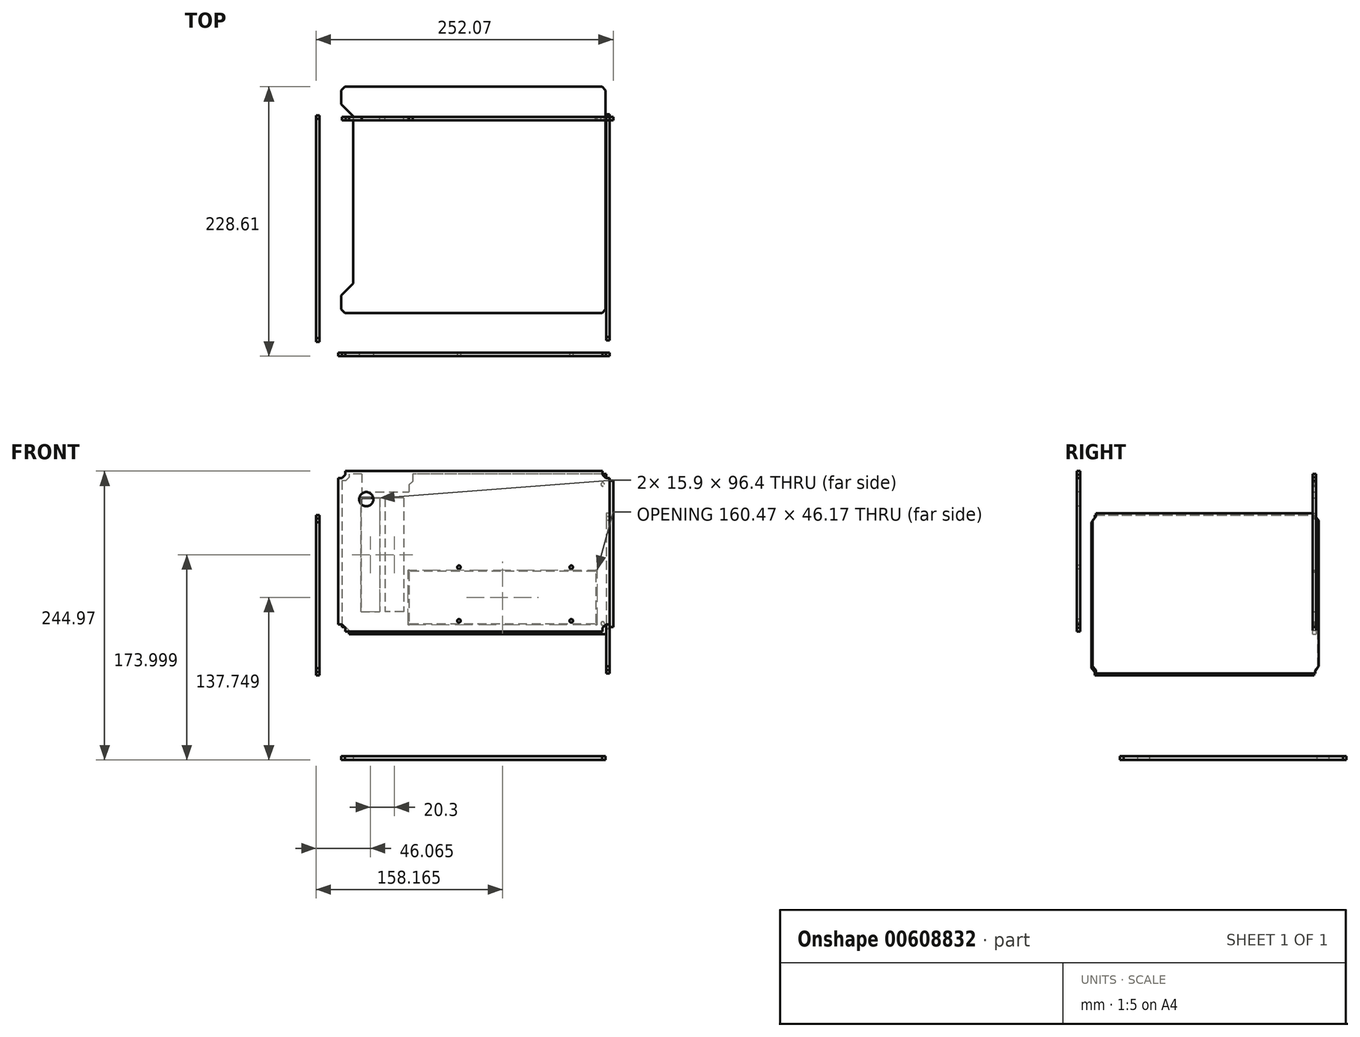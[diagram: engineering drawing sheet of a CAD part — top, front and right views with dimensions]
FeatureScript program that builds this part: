
annotation { "Feature Type Name" : "Feature", "Feature Type Description" : "" }
export const myFeature = defineFeature(function(context is Context, id is Id, definition is map)
    precondition{}
    {
        {
            var Q0;
            Q0=qCreatedBy(makeId("Front.planeOp"),FACE);
            cPlane(context, id + "F0", {"entities" : qUnion([Q0]), "cplaneType" : CPlaneType.OFFSET, "offset" : 80 * mm, "width" : 150 * mm, "height" : 150 * mm});
        }
        {
            var Q0;
            Q0=qCreatedBy(id+"F0.planeOp",FACE);
            var sketch = newSketch(context, id + "F1", { "sketchPlane" : qUnion([Q0])});
            skLineSegment(sketch, "E0.bottom", {"start": v(-107.2, 92.97) * mm, "end": v(122.8, 92.97) * mm});
            skLineSegment(sketch, "E0.top", {"start": v(-107.2, -43.03) * mm, "end": v(122.8, -43.03) * mm});
            skLineSegment(sketch, "E0.left", {"start": v(-107.2, 92.97) * mm, "end": v(-107.2, -43.03) * mm});
            skLineSegment(sketch, "E0.right", {"start": v(122.8, 92.97) * mm, "end": v(122.8, -43.03) * mm});
            skLineSegment(sketch, "E1", {"start": v(116.8, 92.97) * mm, "end": v(116.8, 89.97) * mm});
            skLineSegment(sketch, "E2", {"start": v(116.8, 89.97) * mm, "end": v(119.8, 86.97) * mm});
            skLineSegment(sketch, "E3", {"start": v(119.8, 86.97) * mm, "end": v(122.8, 86.97) * mm});
            skLineSegment(sketch, "E4", {"start": v(122.8, -37.03) * mm, "end": v(119.8, -37.03) * mm});
            skLineSegment(sketch, "E5", {"start": v(119.8, -37.03) * mm, "end": v(116.8, -40.03) * mm});
            skLineSegment(sketch, "E6", {"start": v(116.8, -40.03) * mm, "end": v(116.8, -43.03) * mm});
            skLineSegment(sketch, "E7", {"start": v(-107.2, -37.03) * mm, "end": v(-104.2, -37.03) * mm});
            skLineSegment(sketch, "E8", {"start": v(-104.2, -37.03) * mm, "end": v(-101.2, -40.03) * mm});
            skLineSegment(sketch, "E9", {"start": v(-101.2, -40.03) * mm, "end": v(-101.2, -43.03) * mm});
            skLineSegment(sketch, "E10", {"start": v(-107.2, 86.97) * mm, "end": v(-104.2, 86.97) * mm});
            skLineSegment(sketch, "E11", {"start": v(-104.2, 86.97) * mm, "end": v(-101.2, 89.97) * mm});
            skLineSegment(sketch, "E12", {"start": v(-101.2, 89.97) * mm, "end": v(-101.2, 92.97) * mm});
            skSolve(sketch);
        }
        {
            var Q0;
            {var subQ2=sQuery(id+"F1.wireOp",EDGE,"E1");Q0=makeQuery(id+"F1.imprint","IMPRINT",FACE,{"disambiguationData":[TD([[makeQuery(id+"F1.imprint","IMPRINT",EDGE,{"derivedFrom":subQ2}),-1.0]])]});}
            extrude(context, id + "F2", {"entities" : qUnion([Q0]), "depth" : 3 * mm, "offsetDistance" : 25 * mm});
        }
        {
            var Q0;
            Q0=qCreatedBy(makeId("Right.planeOp"),FACE);
            cPlane(context, id + "F3", {"entities" : qUnion([Q0]), "cplaneType" : CPlaneType.OFFSET, "offset" : 120 * mm, "width" : 150 * mm, "height" : 150 * mm});
        }
        {
            var Q0;
            Q0=qCreatedBy(id+"F3.planeOp",FACE);
            var sketch = newSketch(context, id + "F4", { "sketchPlane" : qUnion([Q0])});
            skLineSegment(sketch, "E13.bottom", {"start": v(-69.71, 57.33) * mm, "end": v(122.29, 57.33) * mm});
            skLineSegment(sketch, "E13.top", {"start": v(-69.71, -78.67) * mm, "end": v(122.29, -78.67) * mm});
            skLineSegment(sketch, "E13.left", {"start": v(-69.71, 57.33) * mm, "end": v(-69.71, -78.67) * mm});
            skLineSegment(sketch, "E13.right", {"start": v(122.29, 57.33) * mm, "end": v(122.29, -78.67) * mm});
            skLineSegment(sketch, "E14", {"start": v(-66.71, 57.33) * mm, "end": v(-66.71, 54.33) * mm});
            skLineSegment(sketch, "E15", {"start": v(-66.71, 54.33) * mm, "end": v(-69.71, 51.33) * mm});
            skLineSegment(sketch, "E16", {"start": v(-69.71, -72.67) * mm, "end": v(-66.71, -75.67) * mm});
            skLineSegment(sketch, "E17", {"start": v(-66.71, -75.67) * mm, "end": v(-66.71, -78.67) * mm});
            skLineSegment(sketch, "E18", {"start": v(119.29, 57.33) * mm, "end": v(119.29, 54.33) * mm});
            skLineSegment(sketch, "E19", {"start": v(119.29, 54.33) * mm, "end": v(122.29, 51.33) * mm});
            skLineSegment(sketch, "E20", {"start": v(122.29, -72.67) * mm, "end": v(119.29, -75.67) * mm});
            skLineSegment(sketch, "E21", {"start": v(119.29, -75.67) * mm, "end": v(119.29, -78.67) * mm});
            skSolve(sketch);
        }
        {
            var Q0;
            {var subQ4=sQuery(id+"F4.wireOp",EDGE,"E14");Q0=makeQuery(id+"F4.imprint","IMPRINT",FACE,{"disambiguationData":[TD([[makeQuery(id+"F4.imprint","IMPRINT",EDGE,{"derivedFrom":subQ4}),1.0]])]});}
            extrude(context, id + "F5", {"entities" : qUnion([Q0]), "depth" : 3 * mm, "offsetDistance" : 25 * mm});
        }
        {
            var Q0;
            Q0=qCreatedBy(makeId("Front.planeOp"),FACE);
            cPlane(context, id + "F6", {"entities" : qUnion([Q0]), "cplaneType" : CPlaneType.OFFSET, "offset" : 120 * mm, "oppositeDirection" : true, "width" : 150 * mm, "height" : 150 * mm});
        }
        {
            var Q0;
            Q0=qCreatedBy(id+"F6.planeOp",FACE);
            var sketch = newSketch(context, id + "F7", { "sketchPlane" : qUnion([Q0])});
            skLineSegment(sketch, "E22.bottom", {"start": v(126.07, 90.7) * mm, "end": v(-103.93, 90.7) * mm});
            skLineSegment(sketch, "E22.top", {"start": v(126.07, -45.3) * mm, "end": v(-103.93, -45.3) * mm});
            skLineSegment(sketch, "E22.left", {"start": v(126.07, 90.7) * mm, "end": v(126.07, -45.3) * mm});
            skLineSegment(sketch, "E22.right", {"start": v(-103.93, 90.7) * mm, "end": v(-103.93, -45.3) * mm});
            skLineSegment(sketch, "E23", {"start": v(126.07, 84.7) * mm, "end": v(123.07, 84.7) * mm});
            skLineSegment(sketch, "E24", {"start": v(123.07, 84.7) * mm, "end": v(120.07, 87.7) * mm});
            skLineSegment(sketch, "E25", {"start": v(120.07, 87.7) * mm, "end": v(120.07, 90.7) * mm});
            skLineSegment(sketch, "E26", {"start": v(-97.93, 90.7) * mm, "end": v(-97.93, 87.7) * mm});
            skLineSegment(sketch, "E27", {"start": v(-97.93, 87.7) * mm, "end": v(-100.93, 84.7) * mm});
            skLineSegment(sketch, "E28", {"start": v(-100.93, 84.7) * mm, "end": v(-103.93, 84.7) * mm});
            skLineSegment(sketch, "E29", {"start": v(-97.93, -45.3) * mm, "end": v(-97.93, -42.3) * mm});
            skLineSegment(sketch, "E30", {"start": v(-97.93, -42.3) * mm, "end": v(-100.93, -39.3) * mm});
            skLineSegment(sketch, "E31", {"start": v(-100.93, -39.3) * mm, "end": v(-103.93, -39.3) * mm});
            skLineSegment(sketch, "E32", {"start": v(126.07, -39.3) * mm, "end": v(123.07, -39.3) * mm});
            skLineSegment(sketch, "E33", {"start": v(123.07, -39.3) * mm, "end": v(120.07, -42.3) * mm});
            skLineSegment(sketch, "E34", {"start": v(120.07, -42.3) * mm, "end": v(120.07, -45.3) * mm});
            skLineSegment(sketch, "E35", {"start": v(126.07, -36.3) * mm, "end": v(117.07, -36.3) * mm, "construction": true});
            skCircle(sketch, "E36", {"center": v(117.07, -36.3) * mm, "radius": 1.5 * mm});
            skLineSegment(sketch, "E37", {"start": v(126.07, 81.7) * mm, "end": v(117.07, 81.7) * mm, "construction": true});
            skCircle(sketch, "E38", {"center": v(117.07, 81.7) * mm, "radius": 1.5 * mm});
            skSolve(sketch);
        }
        {
            var Q0;
            {var subQ2=sQuery(id+"F7.wireOp",EDGE,"E23");Q0=makeQuery(id+"F7.imprint","IMPRINT",FACE,{"disambiguationData":[TD([[makeQuery(id+"F7.imprint","IMPRINT",EDGE,{"derivedFrom":subQ2}),1.0]])]});}
            extrude(context, id + "F8", {"entities" : qUnion([Q0]), "depth" : 3 * mm, "offsetDistance" : 25 * mm});
        }
        {
            var Q0;
            Q0=qCreatedBy(makeId("Right.planeOp"),FACE);
            cPlane(context, id + "F9", {"entities" : qUnion([Q0]), "cplaneType" : CPlaneType.OFFSET, "offset" : 126 * mm, "oppositeDirection" : true, "width" : 150 * mm, "height" : 150 * mm});
        }
        {
            var Q0;
            Q0=qCreatedBy(id+"F9.planeOp",FACE);
            var sketch = newSketch(context, id + "F10", { "sketchPlane" : qUnion([Q0])});
            skLineSegment(sketch, "E39.bottom", {"start": v(-70.73, 55.68) * mm, "end": v(121.27, 55.68) * mm});
            skLineSegment(sketch, "E39.top", {"start": v(-70.73, -80.32) * mm, "end": v(121.27, -80.32) * mm});
            skLineSegment(sketch, "E39.left", {"start": v(-70.73, 55.68) * mm, "end": v(-70.73, -80.32) * mm});
            skLineSegment(sketch, "E39.right", {"start": v(121.27, 55.68) * mm, "end": v(121.27, -80.32) * mm});
            skLineSegment(sketch, "E40", {"start": v(121.27, 49.68) * mm, "end": v(118.27, 52.68) * mm});
            skLineSegment(sketch, "E41", {"start": v(118.27, 52.68) * mm, "end": v(118.27, 55.68) * mm});
            skLineSegment(sketch, "E42", {"start": v(-67.73, 55.68) * mm, "end": v(-67.73, 52.68) * mm});
            skLineSegment(sketch, "E43", {"start": v(-67.73, 52.68) * mm, "end": v(-70.73, 49.68) * mm});
            skLineSegment(sketch, "E44", {"start": v(-67.73, -80.32) * mm, "end": v(-67.73, -77.32) * mm});
            skLineSegment(sketch, "E45", {"start": v(-67.73, -77.32) * mm, "end": v(-70.73, -74.32) * mm});
            skLineSegment(sketch, "E46", {"start": v(121.27, -74.32) * mm, "end": v(118.27, -77.32) * mm});
            skLineSegment(sketch, "E47", {"start": v(118.27, -77.32) * mm, "end": v(118.27, -80.32) * mm});
            skSolve(sketch);
        }
        {
            var Q0;
            {var subQ4=sQuery(id+"F10.wireOp",EDGE,"E40");Q0=makeQuery(id+"F10.imprint","IMPRINT",FACE,{"disambiguationData":[TD([[makeQuery(id+"F10.imprint","IMPRINT",EDGE,{"derivedFrom":subQ4}),1.0]])]});}
            extrude(context, id + "F11", {"entities" : qUnion([Q0]), "depth" : 3 * mm, "offsetDistance" : 25 * mm});
        }
        {
            var Q0;
            Q0=qCreatedBy(makeId("Top.planeOp"),FACE);
            cPlane(context, id + "F12", {"entities" : qUnion([Q0]), "cplaneType" : CPlaneType.OFFSET, "offset" : 152 * mm, "oppositeDirection" : true, "width" : 150 * mm, "height" : 150 * mm});
        }
        {
            var Q0;
            Q0=qCreatedBy(id+"F12.planeOp",FACE);
            var sketch = newSketch(context, id + "F13", { "sketchPlane" : qUnion([Q0])});
            skLineSegment(sketch, "E48.bottom", {"start": v(-104.54, -46.39) * mm, "end": v(119.46, -46.39) * mm});
            skLineSegment(sketch, "E48.top", {"start": v(-104.54, 145.61) * mm, "end": v(119.46, 145.61) * mm});
            skLineSegment(sketch, "E48.left", {"start": v(-104.54, -46.39) * mm, "end": v(-104.54, 145.61) * mm});
            skLineSegment(sketch, "E48.right", {"start": v(119.46, -46.39) * mm, "end": v(119.46, 145.61) * mm});
            skLineSegment(sketch, "E49", {"start": v(-104.54, -43.39) * mm, "end": v(-101.54, -46.39) * mm});
            skLineSegment(sketch, "E50", {"start": v(116.46, -46.39) * mm, "end": v(119.46, -43.39) * mm});
            skLineSegment(sketch, "E51", {"start": v(119.46, 142.61) * mm, "end": v(116.46, 145.61) * mm});
            skLineSegment(sketch, "E52", {"start": v(-104.54, 142.61) * mm, "end": v(-101.54, 145.61) * mm});
            skSolve(sketch);
        }
        {
            var Q0;
            {var subQ3=sQuery(id+"F13.wireOp",EDGE,"E49");Q0=makeQuery(id+"F13.imprint","IMPRINT",FACE,{"disambiguationData":[TD([[makeQuery(id+"F13.imprint","IMPRINT",EDGE,{"derivedFrom":subQ3}),1.0]])]});}
            extrude(context, id + "F14", {"entities" : qUnion([Q0]), "depth" : 3 * mm, "offsetDistance" : 25 * mm});
        }
        {
            var Q0;
            Q0=makeQuery(id+"F2.opExtrude","CAP_FACE",FACE,{"disambiguationData":[OSD([sQuery(id+"F1.wireOp",EDGE,"E0.bottom"),sQuery(id+"F1.wireOp",EDGE,"E0.top"),sQuery(id+"F1.wireOp",EDGE,"E0.left"),sQuery(id+"F1.wireOp",EDGE,"E0.right"),sQuery(id+"F1.wireOp",EDGE,"E1"),sQuery(id+"F1.wireOp",EDGE,"E2"),sQuery(id+"F1.wireOp",EDGE,"E3"),sQuery(id+"F1.wireOp",EDGE,"E4"),sQuery(id+"F1.wireOp",EDGE,"E5"),sQuery(id+"F1.wireOp",EDGE,"E6"),sQuery(id+"F1.wireOp",EDGE,"E7"),sQuery(id+"F1.wireOp",EDGE,"E8"),sQuery(id+"F1.wireOp",EDGE,"E9"),sQuery(id+"F1.wireOp",EDGE,"E10"),sQuery(id+"F1.wireOp",EDGE,"E11"),sQuery(id+"F1.wireOp",EDGE,"E12")])],"isStart":false});
            var sketch = newSketch(context, id + "F15", { "sketchPlane" : qUnion([Q0])});
            skLineSegment(sketch, "E53.bottom", {"start": v(-4.82, 11.42) * mm, "end": v(90.43, 11.42) * mm, "construction": true});
            skLineSegment(sketch, "E53.top", {"start": v(-4.82, -34.03) * mm, "end": v(90.43, -34.03) * mm, "construction": true});
            skLineSegment(sketch, "E53.left", {"start": v(-4.82, 11.42) * mm, "end": v(-4.82, -34.03) * mm, "construction": true});
            skLineSegment(sketch, "E53.right", {"start": v(90.43, 11.42) * mm, "end": v(90.43, -34.03) * mm, "construction": true});
            skCircle(sketch, "E54", {"center": v(-4.82, -34.03) * mm, "radius": 1.5 * mm});
            skCircle(sketch, "E55", {"center": v(-4.82, 11.42) * mm, "radius": 1.5 * mm});
            skCircle(sketch, "E56", {"center": v(90.43, 11.42) * mm, "radius": 1.5 * mm});
            skCircle(sketch, "E57", {"center": v(90.43, -34.03) * mm, "radius": 1.5 * mm});
            skCircle(sketch, "E58", {"center": v(-83.42, 69.2) * mm, "radius": 6 * mm});
            skLineSegment(sketch, "E59", {"start": v(-83.42, 69.2) * mm, "end": v(-107.2, 69.2) * mm, "construction": true});
            skLineSegment(sketch, "E60", {"start": v(-83.42, 69.2) * mm, "end": v(-83.42, 92.97) * mm, "construction": true});
            skLineSegment(sketch, "E61", {"start": v(42.8, -34.03) * mm, "end": v(42.8, -43.03) * mm, "construction": true});
            skSolve(sketch);
        }
        {
            var Q0;
            Q0=qSketchRegion(id+"F15",true);
            extrude(context, id + "F16", {"entities" : qUnion([Q0]), "operationType" : NewBodyOperationType.REMOVE, "oppositeDirection" : true, "depth" : 25 * mm, "offsetDistance" : 25 * mm});
        }
        {
            var Q0;
            Q0=makeQuery(id+"F8.opExtrude","CAP_FACE",FACE,{"disambiguationData":[OSD([sQuery(id+"F7.wireOp",EDGE,"E22.bottom"),sQuery(id+"F7.wireOp",EDGE,"E22.top"),sQuery(id+"F7.wireOp",EDGE,"E22.left"),sQuery(id+"F7.wireOp",EDGE,"E22.right"),sQuery(id+"F7.wireOp",EDGE,"E23"),sQuery(id+"F7.wireOp",EDGE,"E24"),sQuery(id+"F7.wireOp",EDGE,"E25"),sQuery(id+"F7.wireOp",EDGE,"E26"),sQuery(id+"F7.wireOp",EDGE,"E27"),sQuery(id+"F7.wireOp",EDGE,"E28"),sQuery(id+"F7.wireOp",EDGE,"E29"),sQuery(id+"F7.wireOp",EDGE,"E30"),sQuery(id+"F7.wireOp",EDGE,"E31"),sQuery(id+"F7.wireOp",EDGE,"E32"),sQuery(id+"F7.wireOp",EDGE,"E33"),sQuery(id+"F7.wireOp",EDGE,"E34")])],"isStart":true});
            var sketch = newSketch(context, id + "F17", { "sketchPlane" : qUnion([Q0])});
            skLineSegment(sketch, "E62", {"start": v(-109.07, -34.3) * mm, "end": v(60.93, -34.3) * mm, "construction": true});
            skLineSegment(sketch, "E63", {"start": v(59.63, -34.3) * mm, "end": v(59.63, -26.2) * mm, "construction": true});
            skLineSegment(sketch, "E64.bottom", {"start": v(67.58, -26.2) * mm, "end": v(67.58, 70.2) * mm});
            skLineSegment(sketch, "E64.top", {"start": v(51.68, -26.2) * mm, "end": v(51.68, 70.2) * mm});
            skLineSegment(sketch, "E64.left", {"start": v(67.58, -26.2) * mm, "end": v(51.68, -26.2) * mm});
            skLineSegment(sketch, "E64.right", {"start": v(67.58, 70.2) * mm, "end": v(51.68, 70.2) * mm});
            skLineSegment(sketch, "E65.bottom", {"start": v(71.98, -26.2) * mm, "end": v(71.98, 70.2) * mm});
            skLineSegment(sketch, "E65.top", {"start": v(87.88, -26.2) * mm, "end": v(87.88, 70.2) * mm});
            skLineSegment(sketch, "E65.left", {"start": v(71.98, -26.2) * mm, "end": v(87.88, -26.2) * mm});
            skLineSegment(sketch, "E65.right", {"start": v(71.98, 70.2) * mm, "end": v(87.88, 70.2) * mm});
            skLineSegment(sketch, "E66", {"start": v(71.98, 70.2) * mm, "end": v(67.58, 70.2) * mm, "construction": true});
            skLineSegment(sketch, "E67.bottom", {"start": v(-111.67, 8.1) * mm, "end": v(-111.67, -36.6) * mm});
            skLineSegment(sketch, "E68", {"start": v(-111.67, -36.6) * mm, "end": v(47.33, -36.6) * mm});
            skLineSegment(sketch, "E69", {"start": v(47.33, -36.6) * mm, "end": v(47.33, 8.1) * mm});
            skLineSegment(sketch, "E70", {"start": v(47.33, 8.1) * mm, "end": v(-111.67, 8.1) * mm});
            skArc(sketch, "E71", {"start": v(-111.67, -35.85) * mm, "mid": v(-112.2, -37.13) * mm, "end": v(-110.92, -36.6) * mm});
            skArc(sketch, "E72", {"start": v(-110.92, 8.1) * mm, "mid": v(-112.2, 8.63) * mm, "end": v(-111.67, 7.35) * mm});
            skArc(sketch, "E73", {"start": v(46.58, -36.6) * mm, "mid": v(47.87, -37.13) * mm, "end": v(47.33, -35.85) * mm});
            skLineSegment(sketch, "E74", {"start": v(47.18, 75.2) * mm, "end": v(87.18, 75.2) * mm});
            skLineSegment(sketch, "E75", {"start": v(51.68, 70.2) * mm, "end": v(51.68, 75.2) * mm, "construction": true});
            skLineSegment(sketch, "E76", {"start": v(47.18, 75.2) * mm, "end": v(47.18, 81.2) * mm});
            skLineSegment(sketch, "E77", {"start": v(47.18, 81.2) * mm, "end": v(44.18, 84.2) * mm});
            skArc(sketch, "E78", {"start": v(47.33, 7.35) * mm, "mid": v(47.87, 8.63) * mm, "end": v(46.58, 8.1) * mm});
            skLineSegment(sketch, "E79", {"start": v(60.93, -34.3) * mm, "end": v(60.93, -45.3) * mm, "construction": true});
            skLineSegment(sketch, "E80", {"start": v(87.18, 75.2) * mm, "end": v(87.18, 90.7) * mm});
            skLineSegment(sketch, "E81", {"start": v(44.18, 84.2) * mm, "end": v(44.18, 90.7) * mm});
            skSolve(sketch);
        }
        {
            var Q0;
            Q0 = qSketchRegion(id + "F17", true);
            var Q1;
            Q1=makeQuery(id+"F17.imprint","IMPRINT",FACE,{"disambiguationData":[TD([[makeQuery(id+"F17.imprint","IMPRINT",EDGE,{"derivedFrom":sQuery(id+"F17.wireOp",EDGE,"E74")}),1.0]])]});
            extrude(context, id + "F18", {"entities" : qUnion([Q0, Q1]), "operationType" : NewBodyOperationType.REMOVE, "oppositeDirection" : true, "depth" : 25 * mm, "offsetDistance" : 25 * mm});
        }
        {
            var Q0;
            Q0=makeQuery(id+"F14.opExtrude","CAP_FACE",FACE,{"disambiguationData":[OSD([sQuery(id+"F13.wireOp",EDGE,"E48.bottom"),sQuery(id+"F13.wireOp",EDGE,"E48.top"),sQuery(id+"F13.wireOp",EDGE,"E48.left"),sQuery(id+"F13.wireOp",EDGE,"E48.right"),sQuery(id+"F13.wireOp",EDGE,"E49"),sQuery(id+"F13.wireOp",EDGE,"E50"),sQuery(id+"F13.wireOp",EDGE,"E51"),sQuery(id+"F13.wireOp",EDGE,"E52")])],"isStart":true});
            var sketch = newSketch(context, id + "F19", { "sketchPlane" : qUnion([Q0])});
            skLineSegment(sketch, "E82", {"start": v(-104.54, 31.39) * mm, "end": v(-94.54, 21.39) * mm});
            skLineSegment(sketch, "E83", {"start": v(-94.54, 21.39) * mm, "end": v(-94.54, -120.61) * mm});
            skLineSegment(sketch, "E84", {"start": v(-94.54, -120.61) * mm, "end": v(-104.54, -130.61) * mm});
            skSolve(sketch);
        }
        {
            var Q0;
            {var subQ0=sQuery(id+"F19.wireOp",EDGE,"E82");Q0=makeQuery(id+"F19.imprint","IMPRINT",FACE,{"disambiguationData":[TD([[makeQuery(id+"F19.imprint","IMPRINT",EDGE,{"derivedFrom":subQ0}),-1.0]])]});}
            extrude(context, id + "F20", {"entities" : qUnion([Q0]), "operationType" : NewBodyOperationType.REMOVE, "oppositeDirection" : true, "depth" : 25 * mm, "offsetDistance" : 25 * mm});
        }
    });
